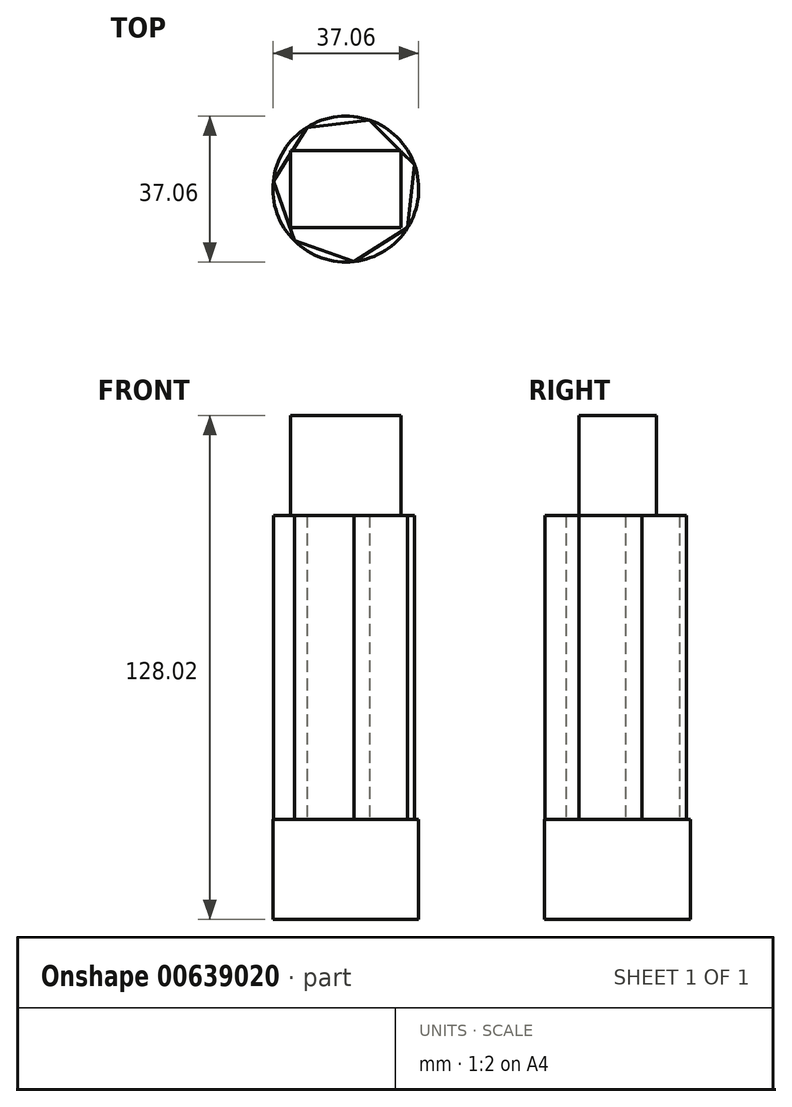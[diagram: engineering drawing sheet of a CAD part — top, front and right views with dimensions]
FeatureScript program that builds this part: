
annotation { "Feature Type Name" : "Feature", "Feature Type Description" : "" }
export const myFeature = defineFeature(function(context is Context, id is Id, definition is map)
    precondition{}
    {
        {
            var Q0;
            Q0=qCreatedBy(makeId("Top.planeOp"),FACE);
            var sketch = newSketch(context, id + "F0", { "sketchPlane" : qUnion([Q0])});
            skCircle(sketch, "E0", {"center": v(0, 0) * mm, "radius": 18.53 * mm});
            skSolve(sketch);
        }
        {
            var Q0;
            Q0 = qSketchRegion(id + "F0", true);
            extrude(context, id + "F1", {"entities" : qUnion([Q0]), "depth" : 25.4 * mm, "offsetDistance" : 25.4 * mm});
        }
        {
            var Q0;
            Q0=makeQuery(id+"F1.opExtrude","CAP_FACE",FACE,{"disambiguationData":[OSD([sQuery(id+"F0.wireOp",EDGE,"E0")])],"isStart":false});
            var sketch = newSketch(context, id + "F2", { "sketchPlane" : qUnion([Q0])});
            skCircle(sketch, "E1.cCircle", {"center": v(0, 0) * mm, "radius": 18.53 * mm, "construction": true});
            skLineSegment(sketch, "E1.0", {"start": v(-9.9, 15.66) * mm, "end": v(6.06, 17.5) * mm});
            skLineSegment(sketch, "E1.1", {"start": v(6.06, 17.5) * mm, "end": v(17.47, 6.17) * mm});
            skLineSegment(sketch, "E1.2", {"start": v(17.47, 6.17) * mm, "end": v(15.72, -9.8) * mm});
            skLineSegment(sketch, "E1.3", {"start": v(15.72, -9.8) * mm, "end": v(2.13, -18.4) * mm});
            skLineSegment(sketch, "E1.4", {"start": v(2.13, -18.4) * mm, "end": v(-13.06, -13.14) * mm});
            skLineSegment(sketch, "E1.5", {"start": v(-13.06, -13.14) * mm, "end": v(-18.42, 2.02) * mm});
            skLineSegment(sketch, "E1.6", {"start": v(-18.42, 2.02) * mm, "end": v(-9.9, 15.66) * mm});
            skSolve(sketch);
        }
        {
            var Q0;
            Q0 = qSketchRegion(id + "F2", true);
            extrude(context, id + "F3", {"entities" : qUnion([Q0]), "operationType" : NewBodyOperationType.ADD, "depth" : 77.22 * mm, "offsetDistance" : 25.4 * mm});
        }
        {
            var Q0;
            Q0=makeQuery(id+"F3.opExtrude","CAP_FACE",FACE,{"disambiguationData":[OSD([sQuery(id+"F2.wireOp",EDGE,"E1.0"),sQuery(id+"F2.wireOp",EDGE,"E1.1"),sQuery(id+"F2.wireOp",EDGE,"E1.2"),sQuery(id+"F2.wireOp",EDGE,"E1.3"),sQuery(id+"F2.wireOp",EDGE,"E1.4"),sQuery(id+"F2.wireOp",EDGE,"E1.5"),sQuery(id+"F2.wireOp",EDGE,"E1.6")])],"isStart":false});
            var sketch = newSketch(context, id + "F4", { "sketchPlane" : qUnion([Q0])});
            skLineSegment(sketch, "E2", {"start": v(8.93, -1.82) * mm, "end": v(-34.47, 58.2) * mm});
            skPoint(sketch, "E2.startSnap0", {"position": v(8.93, -14.1) * mm});
            skPoint(sketch, "E2.startSnap1", {"position": v(16.6, -1.82) * mm});
            skLineSegment(sketch, "E3", {"start": v(-34.47, 58.2) * mm, "end": v(-13.06, -13.14) * mm});
            skLineSegment(sketch, "E4", {"start": v(-13.06, -13.14) * mm, "end": v(-34.47, 58.2) * mm});
            skSolve(sketch);
        }
        {
            var Q0;
            {var subQ0=makeQuery(id+"F3.opExtrude","CAP_EDGE",EDGE,{"disambiguationData":[OSD([sQuery(id+"F2.wireOp",EDGE,"E1.1")])],"isStart":false});Q0=makeQuery(id+"F4.imprint","IMPRINT",FACE,{"disambiguationData":[TD([[makeQuery(id+"F4.imprint","IMPRINT",EDGE,{"derivedFrom":subQ0}),-1.0]])]});}
            var sketch = newSketch(context, id + "F5", { "sketchPlane" : qUnion([Q0])});
            skLineSegment(sketch, "E5.bottom", {"start": v(14.06, 9.82) * mm, "end": v(-14.06, 9.82) * mm});
            skLineSegment(sketch, "E5.top", {"start": v(14.06, -9.82) * mm, "end": v(-14.06, -9.82) * mm});
            skLineSegment(sketch, "E5.left", {"start": v(14.06, 9.82) * mm, "end": v(14.06, -9.82) * mm});
            skLineSegment(sketch, "E5.right", {"start": v(-14.06, 9.82) * mm, "end": v(-14.06, -9.82) * mm});
            skPoint(sketch, "E5.middle", {"position": v(0, 0) * mm});
            skSolve(sketch);
        }
        {
            var Q0;
            Q0 = qSketchRegion(id + "F5", true);
            extrude(context, id + "F6", {"entities" : qUnion([Q0]), "operationType" : NewBodyOperationType.ADD, "depth" : 25.4 * mm, "offsetDistance" : 25.4 * mm});
        }
    });
